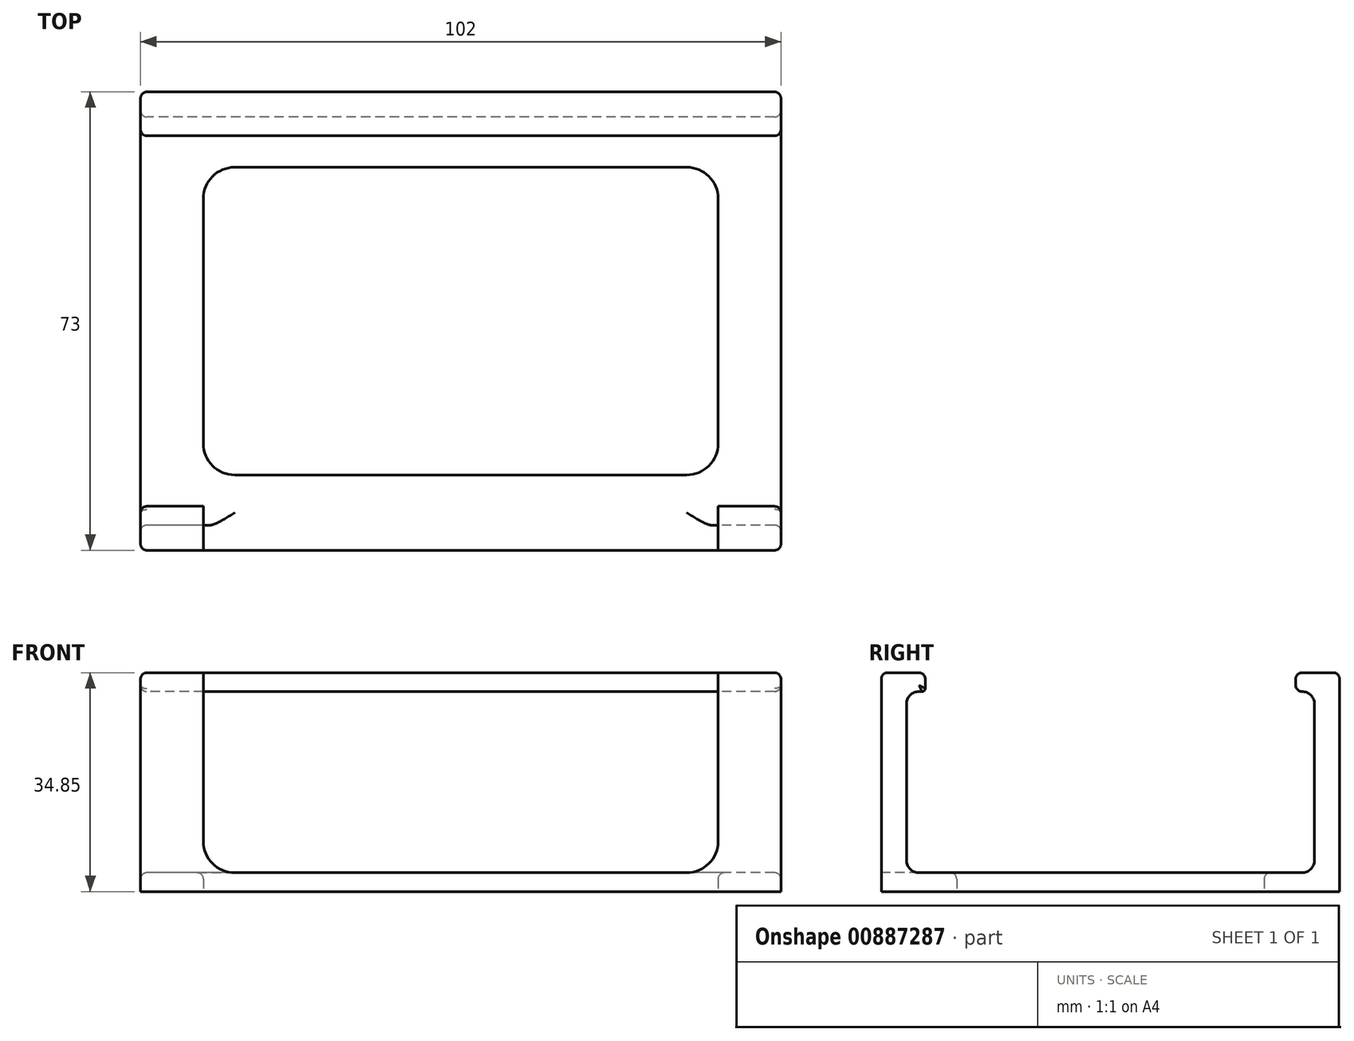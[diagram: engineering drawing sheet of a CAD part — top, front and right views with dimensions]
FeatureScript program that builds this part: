
annotation { "Feature Type Name" : "Feature", "Feature Type Description" : "" }
export const myFeature = defineFeature(function(context is Context, id is Id, definition is map)
    precondition{}
    {
        {
            var Q0;
            Q0=qCreatedBy(makeId("Right.planeOp"),FACE);
            var sketch = newSketch(context, id + "F0", { "sketchPlane" : qUnion([Q0])});
            skLineSegment(sketch, "E0", {"start": v(0, 0) * mm, "end": v(32.5, 0) * mm, "construction": true});
            skLineSegment(sketch, "E1", {"start": v(32.5, 0) * mm, "end": v(32.5, 28.85) * mm, "construction": true});
            skLineSegment(sketch, "E2", {"start": v(32.5, 28.85) * mm, "end": v(-32.5, 28.85) * mm, "construction": true});
            skLineSegment(sketch, "E3", {"start": v(-32.5, 28.85) * mm, "end": v(-32.5, 0) * mm, "construction": true});
            skLineSegment(sketch, "E4", {"start": v(-32.5, 0) * mm, "end": v(0, 0) * mm, "construction": true});
            skLineSegment(sketch, "E5.bottom", {"start": v(-32.5, 0) * mm, "end": v(32.5, 0) * mm, "construction": true});
            skLineSegment(sketch, "E5.top", {"start": v(-32.5, -3) * mm, "end": v(32.5, -3) * mm, "construction": true});
            skLineSegment(sketch, "E5.left", {"start": v(-32.5, 0) * mm, "end": v(-32.5, -3) * mm, "construction": true});
            skLineSegment(sketch, "E5.right", {"start": v(32.5, 0) * mm, "end": v(32.5, -3) * mm, "construction": true});
            skLineSegment(sketch, "E6", {"start": v(0, -3) * mm, "end": v(-36.5, -3) * mm});
            skLineSegment(sketch, "E7", {"start": v(-36.5, -3) * mm, "end": v(-36.5, 31.85) * mm});
            skLineSegment(sketch, "E8", {"start": v(-36.5, 31.85) * mm, "end": v(-29.5, 31.85) * mm});
            skLineSegment(sketch, "E9", {"start": v(-29.5, 31.85) * mm, "end": v(-29.5, 28.85) * mm});
            skLineSegment(sketch, "E10", {"start": v(-29.5, 28.85) * mm, "end": v(-32.5, 28.85) * mm});
            skLineSegment(sketch, "E11", {"start": v(-32.5, 0) * mm, "end": v(0, 0) * mm});
            skLineSegment(sketch, "E12", {"start": v(-32.5, 28.85) * mm, "end": v(-32.5, 0) * mm});
            skLineSegment(sketch, "E13", {"start": v(0, 0) * mm, "end": v(32.5, 0) * mm});
            skLineSegment(sketch, "E14", {"start": v(32.5, 28.85) * mm, "end": v(29.5, 28.85) * mm});
            skLineSegment(sketch, "E15", {"start": v(29.5, 28.85) * mm, "end": v(29.5, 31.85) * mm});
            skLineSegment(sketch, "E16", {"start": v(29.5, 31.85) * mm, "end": v(36.5, 31.85) * mm});
            skLineSegment(sketch, "E17", {"start": v(36.5, 31.85) * mm, "end": v(36.5, -3) * mm});
            skLineSegment(sketch, "E18", {"start": v(36.5, -3) * mm, "end": v(0, -3) * mm});
            skLineSegment(sketch, "E19", {"start": v(32.5, 0) * mm, "end": v(32.5, 28.85) * mm});
            skSolve(sketch);
        }
        {
            var Q0;
            Q0=makeQuery(id+"F0.imprint","IMPRINT",FACE,{"disambiguationData":[TD([[makeQuery(id+"F0.imprint","IMPRINT",EDGE,{"derivedFrom":sQuery(id+"F0.wireOp",EDGE,"E6")}),-1.0]])]});
            extrude(context, id + "F1", {"entities" : qUnion([Q0]), "depth" : 102 * mm, "offsetDistance" : 25 * mm});
        }
        {
            var Q0;
            Q0=makeQuery(id+"F1.opExtrude","SWEPT_FACE",FACE,{"disambiguationData":[OSD([sQuery(id+"F0.wireOp",EDGE,"E6")])]});
            var sketch = newSketch(context, id + "F2", { "sketchPlane" : qUnion([Q0])});
            skLineSegment(sketch, "E20", {"start": v(0, 36.5) * mm, "end": v(10, 36.5) * mm, "construction": true});
            skLineSegment(sketch, "E21", {"start": v(10, -24.5) * mm, "end": v(92, -24.5) * mm, "construction": true});
            skLineSegment(sketch, "E22.top", {"start": v(10, -24.5) * mm, "end": v(92, -24.5) * mm});
            skPoint(sketch, "E23", {"position": v(10, 24.5) * mm});
            skLineSegment(sketch, "E24", {"start": v(10, -24.5) * mm, "end": v(10, 24.5) * mm});
            skLineSegment(sketch, "E25", {"start": v(92, 24.5) * mm, "end": v(10, 24.5) * mm});
            skLineSegment(sketch, "E26", {"start": v(92, 24.5) * mm, "end": v(92, -24.5) * mm});
            skSolve(sketch);
        }
        {
            var Q0;
            {var subQ0=sQuery(id+"F0.wireOp",EDGE,"E12");var subQ1=sQuery(id+"F0.wireOp",EDGE,"E10");Q0=makeQuery(id+"FhsRjMyAQ780hr1_1.boolean.opBoolean","SPLIT",EDGE,{"disambiguationData":[TD([makeQuery(id+"FhsRjMyAQ780hr1_1.opExtrude","SWEPT_FACE",FACE,{"disambiguationData":[OSD([sQuery(id+"F2.wireOp",EDGE,"E22.right")])]})])],"derivedFrom":makeQuery(id+"F1.opExtrude","SWEPT_EDGE",EDGE,{"disambiguationData":[OSD([subQ1,subQ0])]})});}
            var Q1;
            {var subQ0=sQuery(id+"F0.wireOp",EDGE,"E12");var subQ1=sQuery(id+"F0.wireOp",EDGE,"E10");Q1=makeQuery(id+"FhsRjMyAQ780hr1_1.boolean.opBoolean","SPLIT",EDGE,{"disambiguationData":[TD([makeQuery(id+"FhsRjMyAQ780hr1_1.opExtrude","SWEPT_FACE",FACE,{"disambiguationData":[OSD([sQuery(id+"F2.wireOp",EDGE,"E22.left")])]})])],"derivedFrom":makeQuery(id+"F1.opExtrude","SWEPT_EDGE",EDGE,{"disambiguationData":[OSD([subQ1,subQ0])]})});}
            var Q2;
            Q2=makeQuery(id+"F1.opExtrude","SWEPT_EDGE",EDGE,{"disambiguationData":[OSD([sQuery(id+"F0.wireOp",EDGE,"E14"),sQuery(id+"F0.wireOp",EDGE,"E19")])]});
            var Q3;
            Q3=makeQuery(id+"F1.opExtrude","SWEPT_EDGE",EDGE,{"disambiguationData":[OSD([sQuery(id+"F0.wireOp",EDGE,"E13"),sQuery(id+"F0.wireOp",EDGE,"E19")])]});
            var Q4;
            {var subQ1=sQuery(id+"F0.wireOp",EDGE,"E12");var subQ2=sQuery(id+"F0.wireOp",EDGE,"E11");Q4=makeQuery(id+"FhsRjMyAQ780hr1_1.boolean.opBoolean","SPLIT",EDGE,{"disambiguationData":[TD([makeQuery(id+"FhsRjMyAQ780hr1_1.opExtrude","SWEPT_FACE",FACE,{"disambiguationData":[OSD([sQuery(id+"F2.wireOp",EDGE,"E22.right")])]})])],"derivedFrom":makeQuery(id+"F1.opExtrude","SWEPT_EDGE",EDGE,{"disambiguationData":[OSD([subQ2,subQ1])]})});}
            var Q5;
            {var subQ1=sQuery(id+"F0.wireOp",EDGE,"E12");var subQ2=sQuery(id+"F0.wireOp",EDGE,"E11");Q5=makeQuery(id+"FhsRjMyAQ780hr1_1.boolean.opBoolean","SPLIT",EDGE,{"disambiguationData":[TD([makeQuery(id+"FhsRjMyAQ780hr1_1.opExtrude","SWEPT_FACE",FACE,{"disambiguationData":[OSD([sQuery(id+"F2.wireOp",EDGE,"E22.left")])]})])],"derivedFrom":makeQuery(id+"F1.opExtrude","SWEPT_EDGE",EDGE,{"disambiguationData":[OSD([subQ2,subQ1])]})});}
            fillet(context, id + "F3", {"entities" : qUnion([Q0, Q1, Q2, Q3, Q4, Q5]), "radius" : 2 * mm, "tangentPropagation" : true, "allowEdgeOverflow" : false});
        }
        {
            var Q0;
            Q0=makeQuery(id+"F1.opExtrude","SWEPT_EDGE",EDGE,{"disambiguationData":[OSD([sQuery(id+"F0.wireOp",EDGE,"E16"),sQuery(id+"F0.wireOp",EDGE,"E17")])]});
            var Q1;
            {var subQ0=sQuery(id+"F0.wireOp",EDGE,"E9");var subQ1=sQuery(id+"F0.wireOp",EDGE,"E8");Q1=makeQuery(id+"FhsRjMyAQ780hr1_1.boolean.opBoolean","SPLIT",EDGE,{"disambiguationData":[TD([makeQuery(id+"FhsRjMyAQ780hr1_1.opExtrude","SWEPT_FACE",FACE,{"disambiguationData":[OSD([sQuery(id+"F2.wireOp",EDGE,"E22.right")])]})])],"derivedFrom":makeQuery(id+"F1.opExtrude","SWEPT_EDGE",EDGE,{"disambiguationData":[OSD([subQ1,subQ0])]})});}
            var Q2;
            {var subQ0=sQuery(id+"F0.wireOp",EDGE,"E9");var subQ1=sQuery(id+"F0.wireOp",EDGE,"E8");Q2=makeQuery(id+"FhsRjMyAQ780hr1_1.boolean.opBoolean","SPLIT",EDGE,{"disambiguationData":[TD([makeQuery(id+"FhsRjMyAQ780hr1_1.opExtrude","SWEPT_FACE",FACE,{"disambiguationData":[OSD([sQuery(id+"F2.wireOp",EDGE,"E22.left")])]})])],"derivedFrom":makeQuery(id+"F1.opExtrude","SWEPT_EDGE",EDGE,{"disambiguationData":[OSD([subQ1,subQ0])]})});}
            var Q3;
            Q3=makeQuery(id+"F1.opExtrude","SWEPT_EDGE",EDGE,{"disambiguationData":[OSD([sQuery(id+"F0.wireOp",EDGE,"E15"),sQuery(id+"F0.wireOp",EDGE,"E16")])]});
            var Q4;
            Q4=makeQuery(id+"F1.opExtrude","SWEPT_EDGE",EDGE,{"disambiguationData":[OSD([sQuery(id+"F0.wireOp",EDGE,"E14"),sQuery(id+"F0.wireOp",EDGE,"E15")])]});
            fillet(context, id + "F4", {"entities" : qUnion([Q0, Q1, Q2, Q3, Q4]), "radius" : 1 * mm, "tangentPropagation" : true, "allowEdgeOverflow" : false});
        }
        {
            var Q0;
            {var subQ0=sQuery(id+"F0.wireOp",EDGE,"E10");var subQ1=sQuery(id+"F0.wireOp",EDGE,"E9");Q0=makeQuery(id+"FhsRjMyAQ780hr1_1.boolean.opBoolean","SPLIT",EDGE,{"disambiguationData":[TD([makeQuery(id+"FhsRjMyAQ780hr1_1.opExtrude","SWEPT_FACE",FACE,{"disambiguationData":[OSD([sQuery(id+"F2.wireOp",EDGE,"E22.left")])]})])],"derivedFrom":makeQuery(id+"F1.opExtrude","SWEPT_EDGE",EDGE,{"disambiguationData":[OSD([subQ1,subQ0])]})});}
            var Q1;
            {var subQ0=sQuery(id+"F0.wireOp",EDGE,"E10");var subQ1=sQuery(id+"F0.wireOp",EDGE,"E9");Q1=makeQuery(id+"FhsRjMyAQ780hr1_1.boolean.opBoolean","SPLIT",EDGE,{"disambiguationData":[TD([makeQuery(id+"FhsRjMyAQ780hr1_1.opExtrude","SWEPT_FACE",FACE,{"disambiguationData":[OSD([sQuery(id+"F2.wireOp",EDGE,"E22.right")])]})])],"derivedFrom":makeQuery(id+"F1.opExtrude","SWEPT_EDGE",EDGE,{"disambiguationData":[OSD([subQ1,subQ0])]})});}
            fillet(context, id + "F5", {"entities" : qUnion([Q0, Q1]), "radius" : .5 * mm, "tangentPropagation" : true, "allowEdgeOverflow" : false});
        }
        {
            var Q0;
            Q0 = qSketchRegion(id + "F2", true);
            extrude(context, id + "F6", {"entities" : qUnion([Q0]), "operationType" : NewBodyOperationType.REMOVE, "oppositeDirection" : true, "depth" : 5 * mm, "offsetDistance" : 25 * mm});
        }
        {
            var Q0;
            Q0=makeQuery(id+"F1.opExtrude","SWEPT_FACE",FACE,{"disambiguationData":[OSD([sQuery(id+"F0.wireOp",EDGE,"E7")])]});
            var sketch = newSketch(context, id + "F7", { "sketchPlane" : qUnion([Q0])});
            skPoint(sketch, "E27", {"position": v(10, -3) * mm});
            skPoint(sketch, "E28", {"position": v(92, -3) * mm});
            skPoint(sketch, "E29", {"position": v(92, 31.85) * mm});
            skPoint(sketch, "E30", {"position": v(10, 31.85) * mm});
            skLineSegment(sketch, "E31.bottom", {"start": v(10, 31.85) * mm, "end": v(92, 31.85) * mm, "construction": true});
            skLineSegment(sketch, "E31.top", {"start": v(10, -3) * mm, "end": v(92, -3) * mm, "construction": true});
            skLineSegment(sketch, "E31.left", {"start": v(10, 31.85) * mm, "end": v(10, -3) * mm, "construction": true});
            skLineSegment(sketch, "E31.right", {"start": v(92, 31.85) * mm, "end": v(92, -3) * mm, "construction": true});
            skPoint(sketch, "E32", {"position": v(10, 0) * mm});
            skPoint(sketch, "E33", {"position": v(92, 0) * mm});
            skLineSegment(sketch, "E34.bottom", {"start": v(10, 0) * mm, "end": v(92, 0) * mm});
            skLineSegment(sketch, "E34.top", {"start": v(10, 31.85) * mm, "end": v(92, 31.85) * mm});
            skLineSegment(sketch, "E34.left", {"start": v(10, 0) * mm, "end": v(10, 31.85) * mm});
            skLineSegment(sketch, "E34.right", {"start": v(92, 0) * mm, "end": v(92, 31.85) * mm});
            skSolve(sketch);
        }
        {
            var Q0;
            Q0=makeQuery(id+"F7.imprint","IMPRINT",FACE,{"disambiguationData":[TD([[makeQuery(id+"F7.imprint","IMPRINT",EDGE,{"derivedFrom":sQuery(id+"F7.wireOp",EDGE,"E34.bottom")}),1.0]])]});
            extrude(context, id + "F8", {"entities" : qUnion([Q0]), "operationType" : NewBodyOperationType.REMOVE, "oppositeDirection" : true, "depth" : 9.5 * mm, "offsetDistance" : 25 * mm});
        }
        {
            var Q0;
            Q0=makeQuery(id+"F8.boolean.opBoolean","COPY",EDGE,{"derivedFrom":makeQuery(id+"F8.opExtrude","SWEPT_EDGE",EDGE,{"disambiguationData":[OSD([sQuery(id+"F7.wireOp",EDGE,"E34.bottom"),sQuery(id+"F7.wireOp",EDGE,"E34.right")])]})});
            var Q1;
            Q1=makeQuery(id+"F8.boolean.opBoolean","COPY",EDGE,{"derivedFrom":makeQuery(id+"F8.opExtrude","SWEPT_EDGE",EDGE,{"disambiguationData":[OSD([sQuery(id+"F7.wireOp",EDGE,"E34.bottom"),sQuery(id+"F7.wireOp",EDGE,"E34.left")])]})});
            fillet(context, id + "F9", {"entities" : qUnion([Q0, Q1]), "radius" : 5 * mm, "tangentPropagation" : true, "allowEdgeOverflow" : false});
        }
        {
            var Q0;
            {var subQ0=sQuery(id+"F0.wireOp",EDGE,"E8");var subQ1=sQuery(id+"F0.wireOp",EDGE,"E7");Q0=makeQuery(id+"F8.boolean.opBoolean","SPLIT",EDGE,{"disambiguationData":[TD([makeQuery(id+"F8.opExtrude","SWEPT_FACE",FACE,{"disambiguationData":[OSD([sQuery(id+"F7.wireOp",EDGE,"E34.left")])]})])],"derivedFrom":makeQuery(id+"F1.opExtrude","SWEPT_EDGE",EDGE,{"disambiguationData":[OSD([subQ1,subQ0])]})});}
            var Q1;
            {var subQ0=sQuery(id+"F0.wireOp",EDGE,"E8");var subQ1=sQuery(id+"F0.wireOp",EDGE,"E7");Q1=makeQuery(id+"F8.boolean.opBoolean","SPLIT",EDGE,{"disambiguationData":[TD([makeQuery(id+"F8.opExtrude","SWEPT_FACE",FACE,{"disambiguationData":[OSD([sQuery(id+"F7.wireOp",EDGE,"E34.right")])]})])],"derivedFrom":makeQuery(id+"F1.opExtrude","SWEPT_EDGE",EDGE,{"disambiguationData":[OSD([subQ1,subQ0])]})});}
            fillet(context, id + "F10", {"entities" : qUnion([Q0, Q1]), "radius" : 1 * mm, "tangentPropagation" : true, "allowEdgeOverflow" : false});
        }
        {
            var Q0;
            Q0=makeQuery(id+"F6.boolean.opBoolean","COPY",EDGE,{"derivedFrom":makeQuery(id+"F6.opExtrude","SWEPT_EDGE",EDGE,{"disambiguationData":[OSD([sQuery(id+"F2.wireOp",EDGE,"E24"),sQuery(id+"F2.wireOp",EDGE,"E25")])]})});
            var Q1;
            Q1=makeQuery(id+"F6.boolean.opBoolean","COPY",EDGE,{"derivedFrom":makeQuery(id+"F6.opExtrude","SWEPT_EDGE",EDGE,{"disambiguationData":[OSD([sQuery(id+"F2.wireOp",EDGE,"E22.top"),sQuery(id+"F2.wireOp",EDGE,"E24")])]})});
            var Q2;
            Q2=makeQuery(id+"F6.boolean.opBoolean","COPY",EDGE,{"derivedFrom":makeQuery(id+"F6.opExtrude","SWEPT_EDGE",EDGE,{"disambiguationData":[OSD([sQuery(id+"F2.wireOp",EDGE,"E22.top"),sQuery(id+"F2.wireOp",EDGE,"E26")])]})});
            var Q3;
            Q3=makeQuery(id+"F6.boolean.opBoolean","COPY",EDGE,{"derivedFrom":makeQuery(id+"F6.opExtrude","SWEPT_EDGE",EDGE,{"disambiguationData":[OSD([sQuery(id+"F2.wireOp",EDGE,"E25"),sQuery(id+"F2.wireOp",EDGE,"E26")])]})});
            fillet(context, id + "F11", {"entities" : qUnion([Q0, Q1, Q2, Q3]), "radius" : 5 * mm, "tangentPropagation" : true, "allowEdgeOverflow" : false});
        }
        {
            var Q0;
            Q0=makeQuery(id+"F1.opExtrude","CAP_EDGE",EDGE,{"disambiguationData":[OSD([sQuery(id+"F0.wireOp",EDGE,"E7")])],"isStart":true});
            var Q1;
            Q1=makeQuery(id+"F8.boolean.opBoolean","COPY",EDGE,{"derivedFrom":makeQuery(id+"F8.opExtrude","CAP_EDGE",EDGE,{"disambiguationData":[OSD([sQuery(id+"F7.wireOp",EDGE,"E34.left")])],"isStart":true})});
            var Q2;
            Q2=makeQuery(id+"F1.opExtrude","CAP_EDGE",EDGE,{"disambiguationData":[OSD([sQuery(id+"F0.wireOp",EDGE,"E7")])],"isStart":false});
            var Q3;
            Q3=makeQuery(id+"F6.boolean.opBoolean","INTERSECT",EDGE,{"derivedFrom":[makeQuery(id+"F1.opExtrude","SWEPT_FACE",FACE,{"disambiguationData":[OSD([sQuery(id+"F0.wireOp",EDGE,"E11"),sQuery(id+"F0.wireOp",EDGE,"E13")])]}),makeQuery(id+"F6.opExtrude","SWEPT_FACE",FACE,{"disambiguationData":[OSD([sQuery(id+"F2.wireOp",EDGE,"E25")])]})]});
            fillet(context, id + "F12", {"entities" : qUnion([Q0, Q1, Q2, Q3]), "radius" : 1 * mm, "tangentPropagation" : true, "allowEdgeOverflow" : false});
        }
    });
